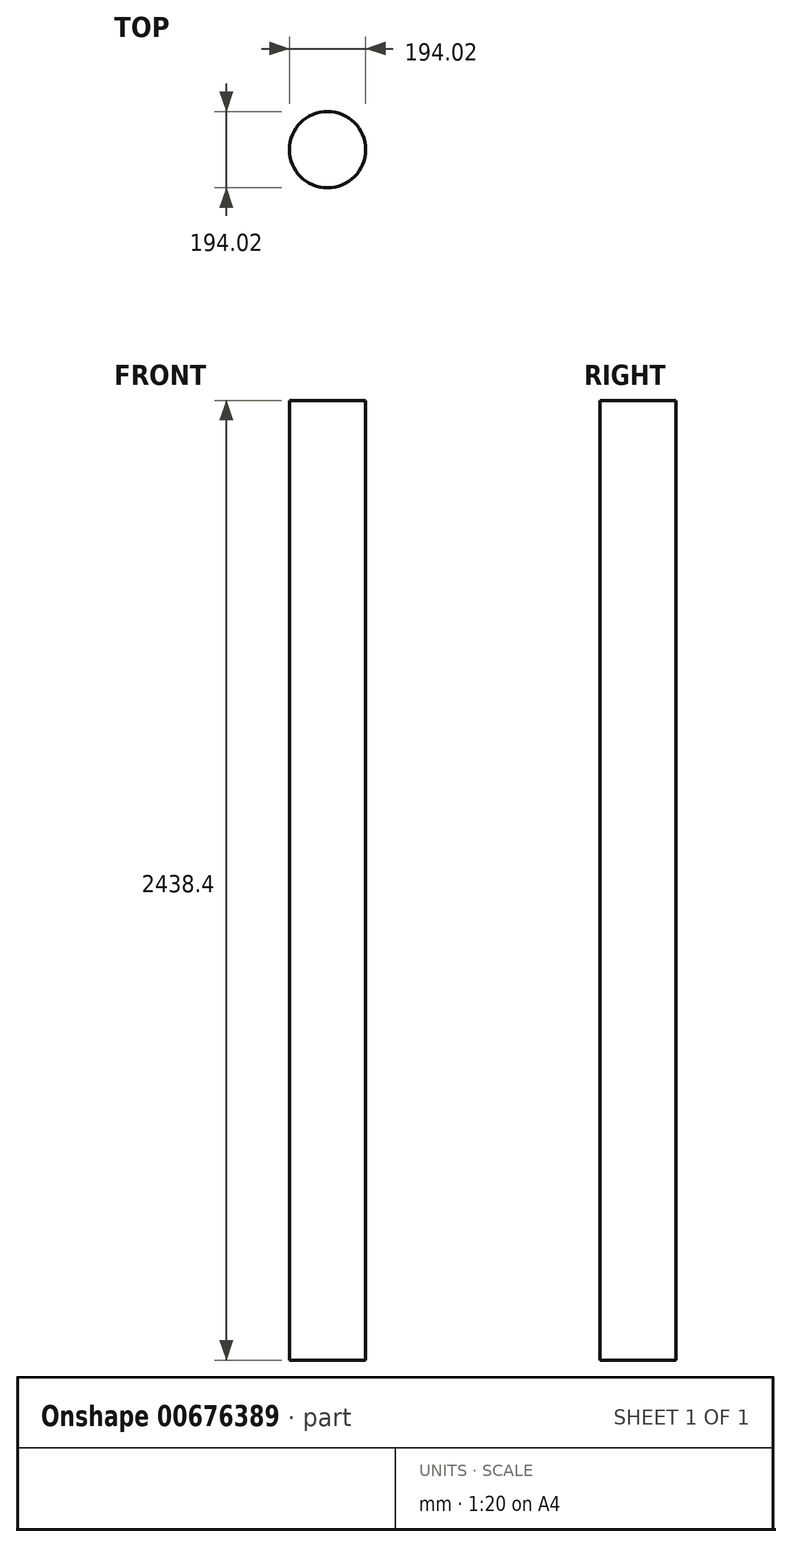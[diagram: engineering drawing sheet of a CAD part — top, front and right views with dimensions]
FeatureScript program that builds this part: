
annotation { "Feature Type Name" : "Feature", "Feature Type Description" : "" }
export const myFeature = defineFeature(function(context is Context, id is Id, definition is map)
    precondition{}
    {
        {
            var Q0;
            Q0=qCreatedBy(makeId("Top.planeOp"),FACE);
            var sketch = newSketch(context, id + "F0", { "sketchPlane" : qUnion([Q0])});
            skCircle(sketch, "E0", {"center": v(0, 0) * mm, "radius": 97 * mm});
            skSolve(sketch);
        }
        {
            var Q0;
            Q0 = qSketchRegion(id + "F0", true);
            extrude(context, id + "F1", {"entities" : qUnion([Q0]), "depth" : 2438.4 * mm, "offsetDistance" : 25.4 * mm});
        }
    });
